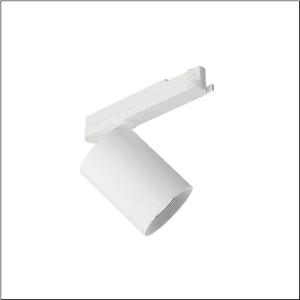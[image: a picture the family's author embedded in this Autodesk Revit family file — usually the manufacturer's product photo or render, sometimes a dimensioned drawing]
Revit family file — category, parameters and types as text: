
# Revit family: spot_21_51se12mbb5b
name_source: partatom
category: Lighting Fixtures
units: mm (PartAtom-declared; Revit-internal decimal feet)

## family parameters
Cut with Voids When Loaded = No
Host = Face
Light Source = No
Part Type = Normal
Room Calculation Point = No
Round Connector Dimension = Use Diameter
Shared = No

## types (1)
- --- (1 x LED, 5300 lm, 41.7 W, 3000K)
    Apparent Load = 42 VA
    CIE Flux Codes = 95 98 99 100 100
    Color Rendering = 90
    Color Temperature = 3000K
    Default Elevation = 1800 mm
    Description = Spot 21, directional spotlight, light control with lens, of PMMA, LED rated luminous flux: 5.100lm, light colour: 930, control gear: ECG Multilumen, with 3-phase adapter, mains connection: 220..240V, AC, 50/60Hz, of aluminium, traffic white (RAL 9016), length: 213mm, diameter: 105mm, protection rating (complete): IP20, insulation class (complete): insulation class I (protective earthing), certification: CE, impact resistance: IK02, permissible ambient temperature for indoor applications: -20..+40°C, packaging unit: 1 piece
    Height = 175 mm
    Lamp = 1 x LED
    Lamp Light Flux = 5300 lm
    Lamp Power = 41.7 W
    Lamp count = 1
    Length = 105 mm
    Luminous efficacy = 127 lm/W
    Manufacturer = Siteco
    ModVariant = No
    Model = 51SE12MBB5B
    Mounting Place = Ceiling
    Mounting Type = Pendant
    Number of Poles = 1
    OnlyDefault = Yes
    Power Factor = 1
    Product Name = Spot 21
    Product group = directional spotlight
    ProductGroupID = 905
    Protection Class = Protection class I
    Protection Degree = IP 20
    RLX_Detail_Level = 1
    RLX_Emergency_Light_Flux = 0 lm
    RLX_Emergency_Type = 0
    RLX_Emergency_Type_DB = No
    RlxData = <blob elided: 17613 chars, md5=21616f77>
    Socket = socket
    Standby Power = 0 W
    System Light Flux = 5300 lm
    System Power = 42 W
    Type Comments = factory setting: luminous flux: 100 % | (ON | ON | ON | ON) | 1050 mA
    Type Image = l_1003976.jpg
    URL = http://relux.com
    VarID = @adj_093809
    Voltage = 0 V
    Weight = 0.00 kg
    Width = 0 mm  [stored 0 ft]

note: [stored X ft] marks values corroborated as IEEE doubles in the binary element streams (Revit-internal decimal feet)

## geometry (parser evidence)
native form markers: Blend x4, Sweep x10
no freeform markers — native parametric forms only
